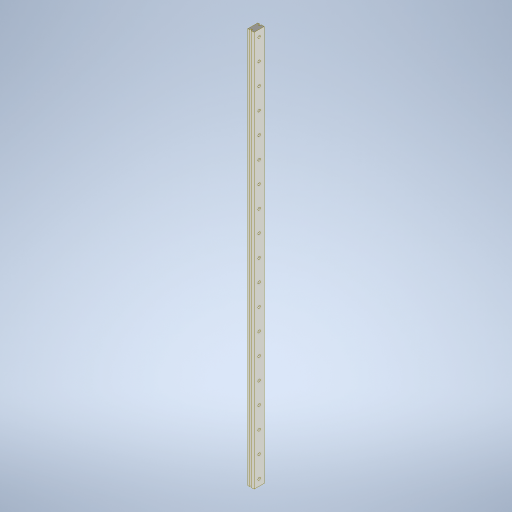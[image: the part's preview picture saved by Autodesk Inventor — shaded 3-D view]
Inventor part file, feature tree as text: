
AUTODESK INVENTOR PART (.ipt)
format: ipt  version: 2023 (Build 270158000, 158)  size: 307,712 bytes
history: native  units: mm
features: sketch x2, other x1, extrude x1, hole x1
ambient origin geometry x8: Origin, YZ Plane, XZ Plane, XY Plane, X Axis, Y Axis, Z Axis, Center Point
bodies: Body1 (feature_tree)
feature tree (5):
  other  "Sólido1"
  extrude  "Extrusão1"  Depth=469.0mm TaperAngle=0.0deg
  hole  "Furo1"  [1 undecoded]
  sketch  "Esboço1"  dims[d0=7.5mm d1=12.0mm d2=8.0mm d3=1.0mm d4=3.5mm d5=0.5mm d6=469.0mm d7=0.0mm]
  sketch  "Esboço2"  dims[d8=190.0mm d10=25.2mm d11=10.0mm d13=10.0mm d18=6.0mm d19=3.0mm d20=13.0mm d21=4.0mm d22=2.0mm d23=90.0deg d24=0.5mm d25=20.594885mm d27=453.6mm d28=469.0mm d29=7.7mm]
note: 1 required parameter value undecoded (feature->parameter linkage not recoverable at this tier; creation-order binding heuristic only, values carry confidence <= 0.55)
